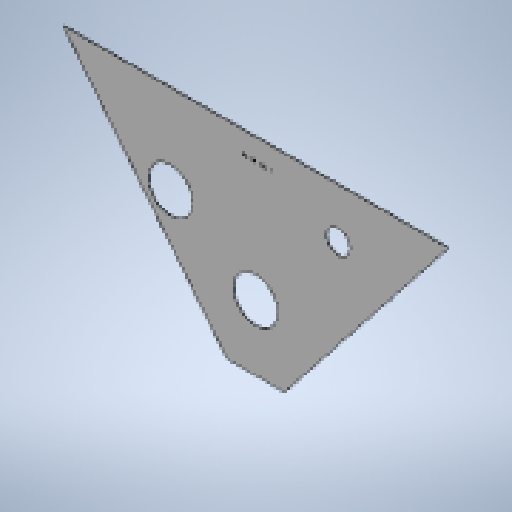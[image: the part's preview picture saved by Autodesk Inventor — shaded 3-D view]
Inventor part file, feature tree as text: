
AUTODESK INVENTOR PART (.ipt)
format: ipt  version: 2025 (Build 290162010, 162A)  size: 271,360 bytes
history: native  units: mm
features: other x3, sketch x3, sheet_metal_op x1, mirror x1, extrude x1, projected_geometry x1
ambient origin geometry x8: Origin, YZ Plane, XZ Plane, XY Plane, X Axis, Y Axis, Z Axis, Center Point
bodies: Solid1 (feature_tree)
feature tree (10):
  sheet_metal_op  "Face1"
  mirror  "Mirror1"
  extrude  "Extrusion1"  Depth=2.0mm
  other  "Mark1"
  sketch  "Sketch1"  dims[d1=735.090647mm d2=2.0mm]
  other  "Plate1"
  sketch  "Sketch2"  dims[d3=2.0mm]
  projected_geometry  "Projected Loop1"
  sketch  "Sketch3"  dims[d5=22.414154mm d6=110.0mm d9=790.0mm d13=169.0mm d14=0.0mm d15=0.0mm d16=250.0mm d17=450.0mm d18=325.0mm d19=31.0mm d20=90.0mm d21=156.0mm d23=315.0mm d24=600.0mm d25=12.0mm d26=110.0mm d28=22.414154mm]
  other  "Definition1"
